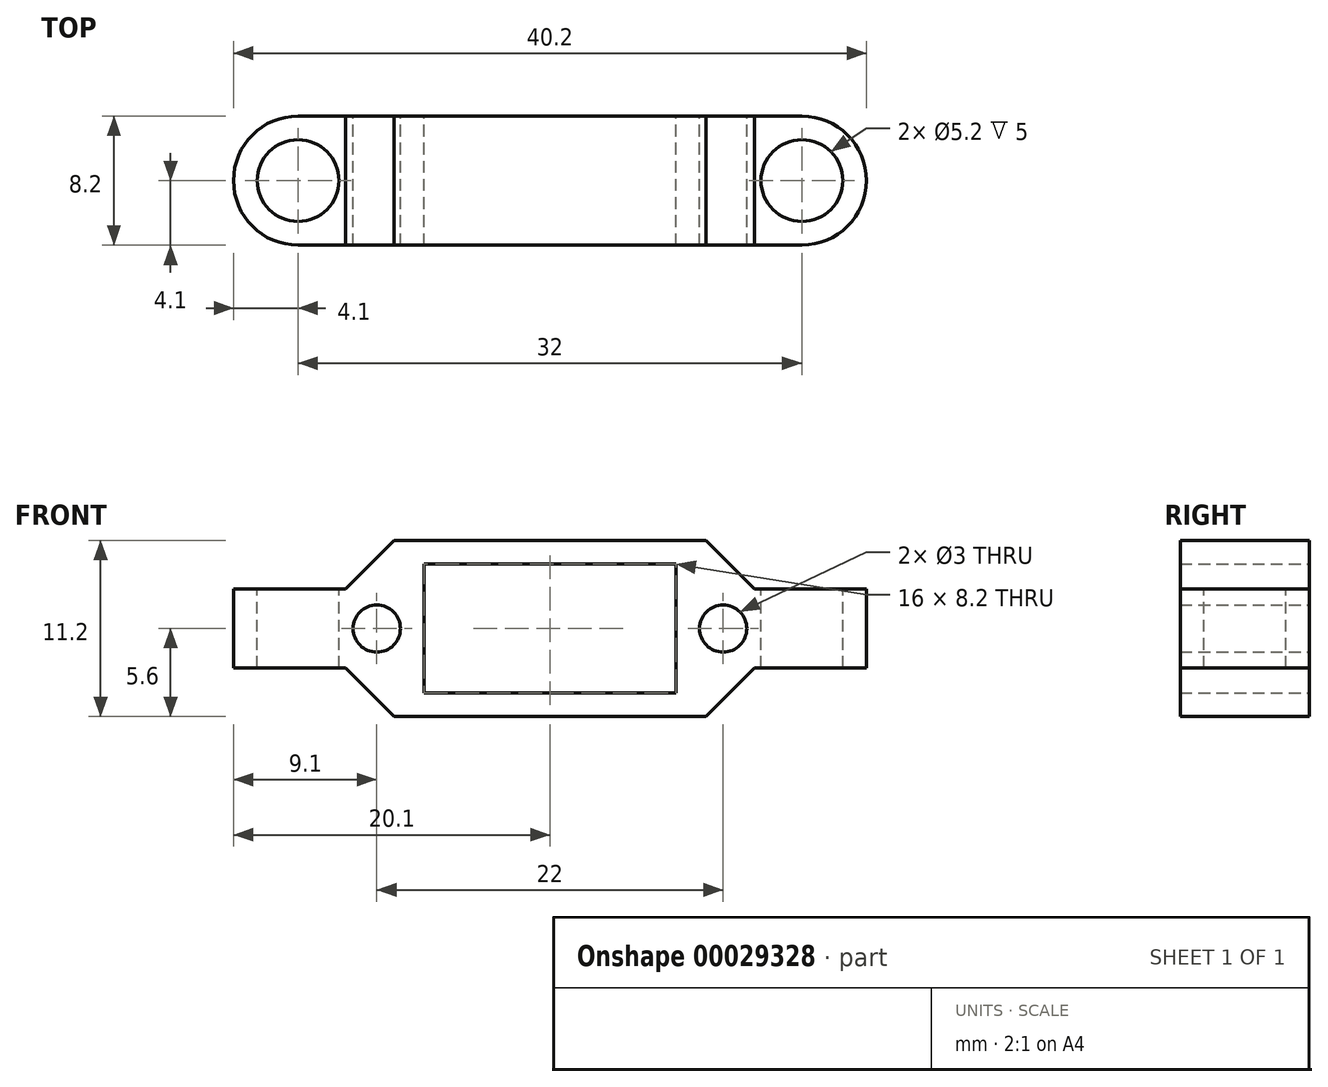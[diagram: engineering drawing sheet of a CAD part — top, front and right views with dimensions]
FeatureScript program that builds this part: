
annotation { "Feature Type Name" : "Feature", "Feature Type Description" : "" }
export const myFeature = defineFeature(function(context is Context, id is Id, definition is map)
    precondition{}
    {
        {
            var Q0;
            Q0=qCreatedBy(makeId("Top.planeOp"),FACE);
            var sketch = newSketch(context, id + "F0", { "sketchPlane" : qUnion([Q0])});
            skCircle(sketch, "E0", {"center": v(-16, -4.1) * mm, "radius": 2.6 * mm});
            skCircle(sketch, "E1.MirrorC", {"center": v(16, -4.1) * mm, "radius": 2.6 * mm});
            skArc(sketch, "E2", {"start": v(-16, 0) * mm, "mid": v(-20.1, -4.1) * mm, "end": v(-16, -8.2) * mm});
            skArc(sketch, "E3.MirrorC", {"start": v(16, 0) * mm, "mid": v(20.1, -4.1) * mm, "end": v(16, -8.2) * mm});
            skLineSegment(sketch, "E4", {"start": v(-16, -8.2) * mm, "end": v(16, -8.2) * mm});
            skLineSegment(sketch, "E5", {"start": v(-16, 0) * mm, "end": v(16, 0) * mm});
            skLineSegment(sketch, "E6", {"start": v(-20.1, -4.1) * mm, "end": v(-20.1, 0) * mm, "construction": true});
            skSolve(sketch);
        }
        {
            var Q0;
            Q0=qCreatedBy(makeId("Front.planeOp"),FACE);
            var sketch = newSketch(context, id + "F1", { "sketchPlane" : qUnion([Q0])});
            skLineSegment(sketch, "E7.rect.bottom", {"start": v(8, 4.1) * mm, "end": v(-8, 4.1) * mm});
            skLineSegment(sketch, "E7.rect.top", {"start": v(8, -4.1) * mm, "end": v(-8, -4.1) * mm});
            skLineSegment(sketch, "E7.rect.left", {"start": v(8, 4.1) * mm, "end": v(8, -4.1) * mm});
            skLineSegment(sketch, "E7.rect.right", {"start": v(-8, 4.1) * mm, "end": v(-8, -4.1) * mm});
            skPoint(sketch, "E7.rect.middle", {"position": v(0, 0) * mm});
            skCircle(sketch, "E8", {"center": v(-11, 0) * mm, "radius": 1.5 * mm});
            skCircle(sketch, "E9.MirrorC", {"center": v(11, 0) * mm, "radius": 1.5 * mm});
            skLineSegment(sketch, "E10", {"start": v(-20.1, 2.5) * mm, "end": v(-20.1, 0) * mm});
            skLineSegment(sketch, "E11", {"start": v(-20.1, 2.5) * mm, "end": v(-13, 2.5) * mm});
            skLineSegment(sketch, "E12", {"start": v(-13, 2.5) * mm, "end": v(-9.9, 5.6) * mm});
            skLineSegment(sketch, "E13", {"start": v(-9.9, 5.6) * mm, "end": v(0, 5.6) * mm});
            skLineSegment(sketch, "E14.MirrorCS", {"start": v(9.9, 5.6) * mm, "end": v(0, 5.6) * mm});
            skLineSegment(sketch, "E15.MirrorCS", {"start": v(13, 2.5) * mm, "end": v(9.9, 5.6) * mm});
            skLineSegment(sketch, "E16.MirrorCS", {"start": v(20.1, 2.5) * mm, "end": v(13, 2.5) * mm});
            skLineSegment(sketch, "E17.MirrorCS", {"start": v(20.1, 2.5) * mm, "end": v(20.1, 0) * mm});
            skLineSegment(sketch, "E18.MirrorCS", {"start": v(-20.1, -2.5) * mm, "end": v(-20.1, 0) * mm});
            skLineSegment(sketch, "E19.MirrorCS", {"start": v(-20.1, -2.5) * mm, "end": v(-13, -2.5) * mm});
            skLineSegment(sketch, "E20.MirrorCS", {"start": v(-13, -2.5) * mm, "end": v(-9.9, -5.6) * mm});
            skLineSegment(sketch, "E21.MirrorCS", {"start": v(-9.9, -5.6) * mm, "end": v(0, -5.6) * mm});
            skLineSegment(sketch, "E22.MirrorCS", {"start": v(9.9, -5.6) * mm, "end": v(0, -5.6) * mm});
            skLineSegment(sketch, "E23.MirrorCS", {"start": v(13, -2.5) * mm, "end": v(9.9, -5.6) * mm});
            skLineSegment(sketch, "E24.MirrorCS", {"start": v(20.1, -2.5) * mm, "end": v(13, -2.5) * mm});
            skLineSegment(sketch, "E25.MirrorCS", {"start": v(20.1, -2.5) * mm, "end": v(20.1, 0) * mm});
            skSolve(sketch);
        }
        {
            var Q0;
            Q0=makeQuery(id+"F1.imprint","IMPRINT",FACE,{"disambiguationData":[TD([[makeQuery(id+"F1.imprint","IMPRINT",EDGE,{"derivedFrom":sQuery(id+"F1.wireOp",EDGE,"E7.rect.bottom")}),-1.0]])]});
            extrude(context, id + "F2", {"entities" : qUnion([Q0]), "depth" : 10 * mm});
        }
        {
            var Q0;
            Q0=makeQuery(id+"F0.imprint","IMPRINT",FACE,{"disambiguationData":[TD([[makeQuery(id+"F0.imprint","IMPRINT",EDGE,{"derivedFrom":sQuery(id+"F0.wireOp",EDGE,"E0")}),-1.0]])]});
            extrude(context, id + "F3", {"entities" : qUnion([Q0]), "operationType" : NewBodyOperationType.INTERSECT, "endBound" : BoundingType.SYMMETRIC, "oppositeDirection" : true, "depth" : 25 * mm});
        }
    });
